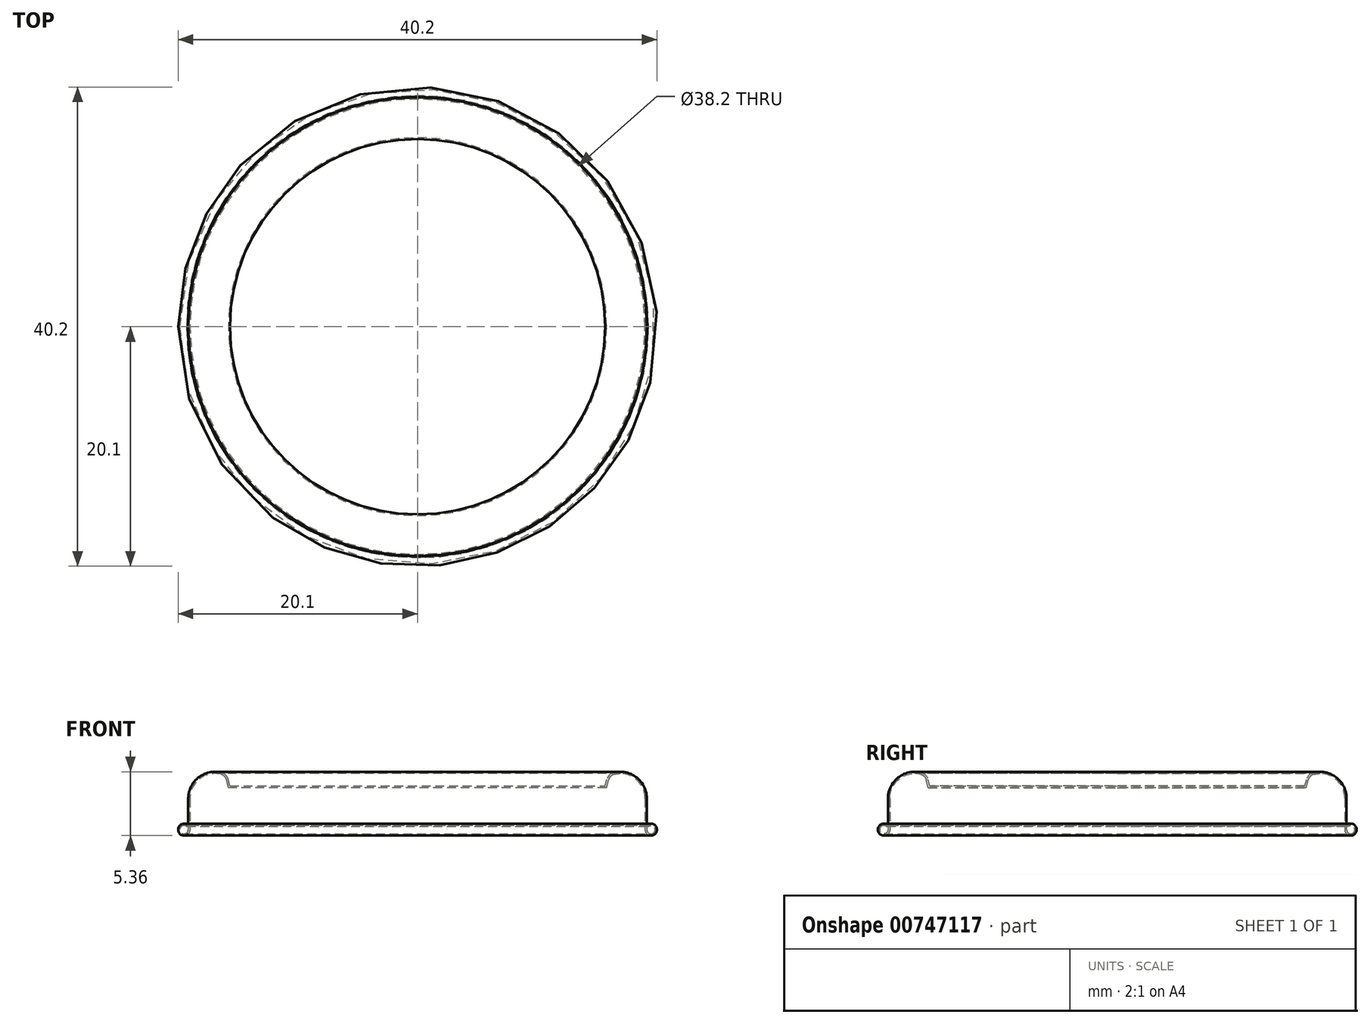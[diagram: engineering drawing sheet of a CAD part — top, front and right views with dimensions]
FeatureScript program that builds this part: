
annotation { "Feature Type Name" : "Feature", "Feature Type Description" : "" }
export const myFeature = defineFeature(function(context is Context, id is Id, definition is map)
    precondition{}
    {
        {
            var Q0;
            Q0=qCreatedBy(makeId("Top.planeOp"),FACE);
            var sketch = newSketch(context, id + "F0", { "sketchPlane" : qUnion([Q0])});
            skCircle(sketch, "E0", {"center": v(0, 0) * mm, "radius": 19.25 * mm});
            skSolve(sketch);
        }
        {
            var Q0;
            Q0=makeQuery(id+"F0.imprint","IMPRINT",FACE,{"disambiguationData":[TD([[makeQuery(id+"F0.imprint","IMPRINT",EDGE,{"derivedFrom":sQuery(id+"F0.wireOp",EDGE,"E0")}),1.0]])]});
            extrude(context, id + "F1", {"entities" : qUnion([Q0]), "depth" : (5.8 - 2.38 - .8) * mm, "offsetDistance" : 25 * mm});
        }
        {
            var Q0;
            Q0=qCreatedBy(makeId("Front.planeOp"),FACE);
            var sketch = newSketch(context, id + "F2", { "sketchPlane" : qUnion([Q0])});
            skArc(sketch, "E1", {"start": v(-19.3, 0.4) * mm, "mid": v(-20.05, -0.22) * mm, "end": v(-19.1, 0) * mm});
            skArc(sketch, "E2", {"start": v(-19.4, 0.28) * mm, "mid": v(-19.91, -0.16) * mm, "end": v(-19.25, 0) * mm});
            skLineSegment(sketch, "E3", {"start": v(-19.25, 0) * mm, "end": v(-19.1, 0) * mm});
            skLineSegment(sketch, "E4", {"start": v(-19.4, 0.28) * mm, "end": v(-19.3, 0.4) * mm});
            skSolve(sketch);
        }
        {
            var Q0;
            Q0=qSketchRegion(id+"F2",true);
            var Q1;
            Q1=makeQuery(id+"F1.opExtrude","CAP_EDGE",EDGE,{"disambiguationData":[OSD([sQuery(id+"F0.wireOp",EDGE,"E0")])],"isStart":true});
            revolve(context, id + "F3", {"operationType" : NewBodyOperationType.ADD, "surfaceOperationType" : NewSurfaceOperationType.NEW, "entities" : qUnion([Q0]), "axis" : qUnion([Q1]), "revolveType" : RevolveType.FULL});
        }
        {
            var Q0;
            Q0=qCreatedBy(makeId("Front.planeOp"),FACE);
            var sketch = newSketch(context, id + "F4", { "sketchPlane" : qUnion([Q0])});
            skArc(sketch, "E5", {"start": v(-16.48, 4.8) * mm, "mid": v(-18.4, 4.38) * mm, "end": v(-19.25, 2.62) * mm});
            skArc(sketch, "E6", {"start": v(-15.9, 4.2) * mm, "mid": v(-16.1, 4.58) * mm, "end": v(-16.48, 4.8) * mm});
            skLineSegment(sketch, "E7", {"start": v(-19.25, 2.62) * mm, "end": v(-15.5, 2.62) * mm});
            skLineSegment(sketch, "E8", {"start": v(-15.9, 4.2) * mm, "end": v(-15.76, 3.66) * mm});
            skLineSegment(sketch, "E9", {"start": v(-15.76, 3.66) * mm, "end": v(0, 3.66) * mm});
            skLineSegment(sketch, "E10", {"start": v(0, 3.66) * mm, "end": v(0, 2.62) * mm});
            skLineSegment(sketch, "E11", {"start": v(0, 2.62) * mm, "end": v(-15.5, 2.62) * mm});
            skSolve(sketch);
        }
        {
            var Q0;
            Q0=makeQuery(id+"F4.imprint","IMPRINT",FACE,{"disambiguationData":[TD([[makeQuery(id+"F4.imprint","IMPRINT",EDGE,{"derivedFrom":sQuery(id+"F4.wireOp",EDGE,"E5")}),1.0]])]});
            var Q1;
            Q1=makeQuery(id+"F1.opExtrude","CAP_EDGE",EDGE,{"disambiguationData":[OSD([sQuery(id+"F0.wireOp",EDGE,"E0")])],"isStart":false});
            revolve(context, id + "F5", {"operationType" : NewBodyOperationType.ADD, "surfaceOperationType" : NewSurfaceOperationType.NEW, "entities" : qUnion([Q0]), "axis" : qUnion([Q1]), "revolveType" : RevolveType.FULL});
        }
        {
            var Q0;
            Q0=makeQuery(id+"F1.opExtrude","CAP_FACE",FACE,{"disambiguationData":[OSD([sQuery(id+"F0.wireOp",EDGE,"E0")])],"isStart":true});
            shell(context, id + "F6", {"entities" : qUnion([Q0]), "thickness" : .15 * mm});
        }
    });
